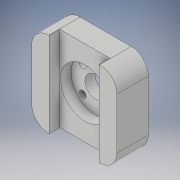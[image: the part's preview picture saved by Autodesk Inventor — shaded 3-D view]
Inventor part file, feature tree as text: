
AUTODESK INVENTOR PART (.ipt)
format: ipt  version: 2018 (Build 220112000, 112)  size: 148,992 bytes
history: native  units: in
note: dims shown in document units (in); Inventor stores cm internally (conversion verified against a paired STEP export)
features: extrude x4, sketch x4, fillet x1
ambient origin geometry x8: Origin, YZ Plane, XZ Plane, XY Plane, X Axis, Y Axis, Z Axis, Center Point
bodies: Solid1 (feature_tree)
feature tree (9):
  extrude  "Extrusion1"  Depth=0.5823in
  extrude  "Extrusion2"  Depth=0.3252in
  extrude  "Extrusion3"  Depth=1.5748in TaperAngle=0.0deg
  extrude  "Extrusion4"  Depth=0.1969in TaperAngle=0.0deg
  fillet  "Fillet1"  Radius=0.3937in
  sketch  "Sketch1"  dims[d0=1.5748in d1=0.5823in]
  sketch  "Sketch2"  dims[d2=0.3252in d3=0.3252in]
  sketch  "Sketch3"  dims[d4=0.1969in d5=1.5748in d6=0.0in]
  sketch  "Sketch4"  dims[d7=0.9055in d8=0.1969in d9=0.0in d10=0.3937in d11=0.1969in d12=0.0in d13=0.2362in d14=0.2362in d15=0.126in d16=1.5748in d18=360.0deg d20=0.1969in d21=0.0in d22=0.315in]
